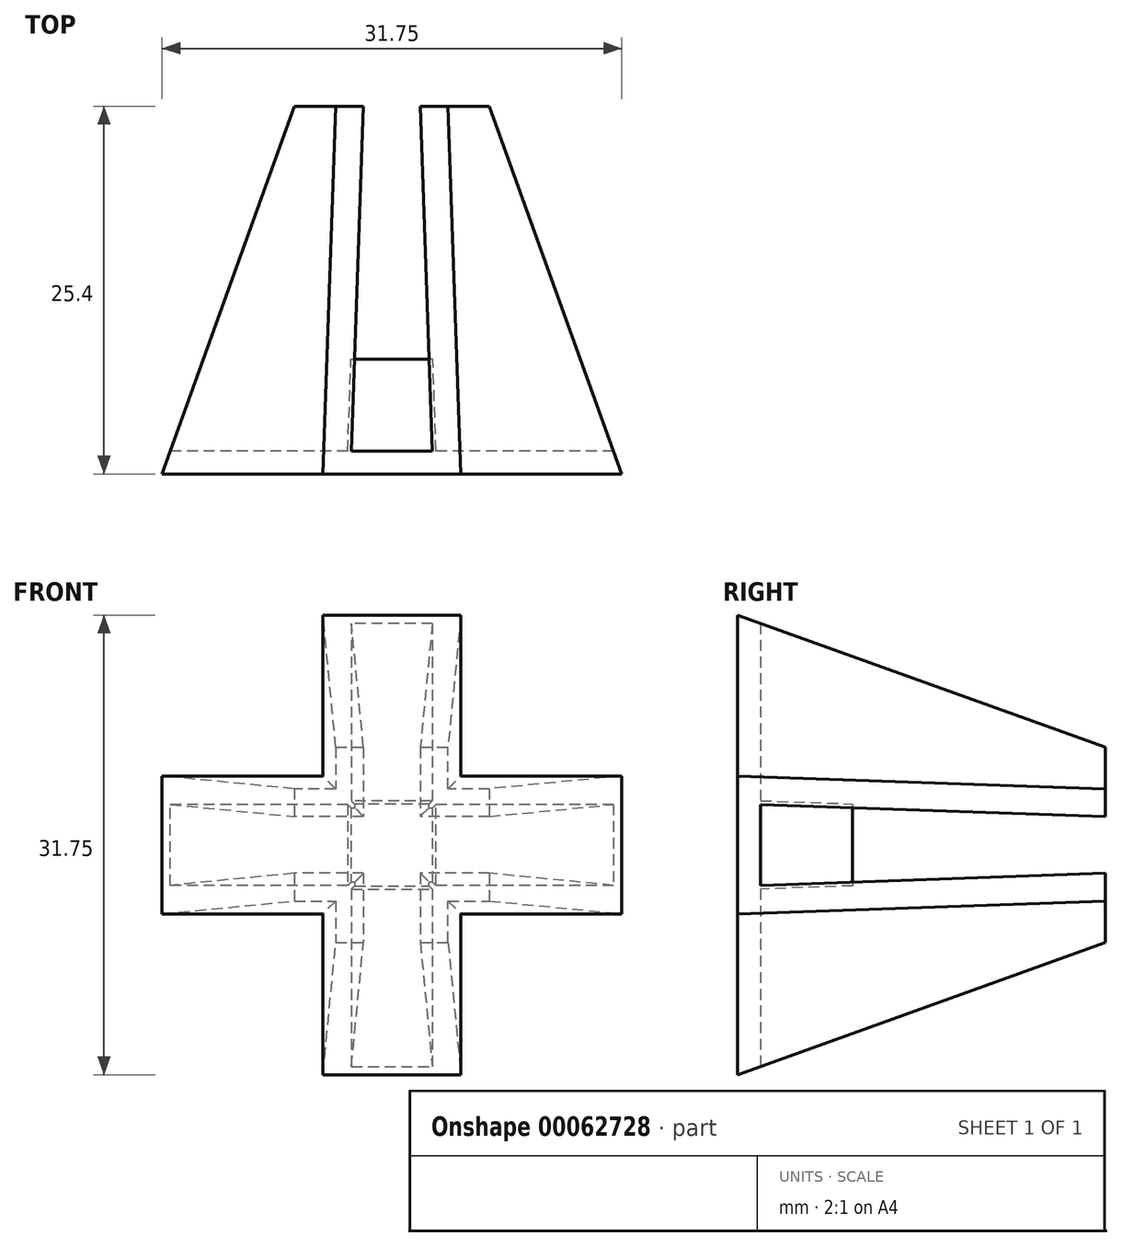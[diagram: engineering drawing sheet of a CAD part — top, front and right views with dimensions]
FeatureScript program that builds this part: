
annotation { "Feature Type Name" : "Feature", "Feature Type Description" : "" }
export const myFeature = defineFeature(function(context is Context, id is Id, definition is map)
    precondition{}
    {
        {
            var Q0;
            Q0=qCreatedBy(makeId("Front.planeOp"),FACE);
            var sketch = newSketch(context, id + "F0", { "sketchPlane" : qUnion([Q0])});
            skLineSegment(sketch, "E0", {"start": v(0, 31.75) * mm, "end": v(9.53, 31.75) * mm});
            skLineSegment(sketch, "E1", {"start": v(9.53, 31.75) * mm, "end": v(9.52, 20.64) * mm});
            skLineSegment(sketch, "E2", {"start": v(9.52, 20.64) * mm, "end": v(20.64, 20.64) * mm});
            skLineSegment(sketch, "E3", {"start": v(20.64, 20.64) * mm, "end": v(20.64, 11.11) * mm});
            skLineSegment(sketch, "E4", {"start": v(20.64, 11.11) * mm, "end": v(9.52, 11.11) * mm});
            skLineSegment(sketch, "E5", {"start": v(9.52, 11.11) * mm, "end": v(9.52, 0) * mm});
            skLineSegment(sketch, "E6", {"start": v(9.52, 0) * mm, "end": v(0, 0) * mm});
            skLineSegment(sketch, "E7", {"start": v(0, 0) * mm, "end": v(0, 11.11) * mm});
            skLineSegment(sketch, "E8", {"start": v(0, 11.11) * mm, "end": v(-11.11, 11.11) * mm});
            skLineSegment(sketch, "E9", {"start": v(-11.11, 11.11) * mm, "end": v(-11.11, 20.64) * mm});
            skLineSegment(sketch, "E10", {"start": v(-11.11, 20.64) * mm, "end": v(0, 20.64) * mm});
            skLineSegment(sketch, "E11", {"start": v(0, 20.64) * mm, "end": v(0, 31.75) * mm});
            skSolve(sketch);
        }
        {
            var Q0;
            Q0=makeQuery(id+"F0.imprint","IMPRINT",FACE,{"disambiguationData":[TD([[makeQuery(id+"F0.imprint","IMPRINT",EDGE,{"derivedFrom":sQuery(id+"F0.wireOp",EDGE,"E0")}),-1.0]])]});
            extrude(context, id + "F1", {"entities" : qUnion([Q0]), "oppositeDirection" : true, "depth" : 25.4 * mm, "hasDraft" : true, "draftAngle" : 2 * degree, "draftPullDirection" : true});
        }
        {
            var Q0;
            Q0=qCreatedBy(makeId("Top.planeOp"),FACE);
            var sketch = newSketch(context, id + "F2", { "sketchPlane" : qUnion([Q0])});
            skLineSegment(sketch, "E12", {"start": v(1.97, 1.59) * mm, "end": v(7.56, 1.59) * mm});
            skLineSegment(sketch, "E13", {"start": v(4.76, 1.59) * mm, "end": v(4.76, 0) * mm, "construction": true});
            skLineSegment(sketch, "E14", {"start": v(1.97, 1.59) * mm, "end": v(2.8, 25.4) * mm});
            skLineSegment(sketch, "E15", {"start": v(2.8, 25.4) * mm, "end": v(6.72, 25.4) * mm});
            skLineSegment(sketch, "E16", {"start": v(6.72, 25.4) * mm, "end": v(7.56, 1.59) * mm});
            skSolve(sketch);
        }
        {
            var Q0;
            Q0=makeQuery(id+"F2.imprint","IMPRINT",FACE,{"disambiguationData":[TD([[makeQuery(id+"F2.imprint","IMPRINT",EDGE,{"derivedFrom":sQuery(id+"F2.wireOp",EDGE,"E12")}),1.0]])]});
            extrude(context, id + "F3", {"entities" : qUnion([Q0]), "operationType" : NewBodyOperationType.REMOVE, "endBound" : BoundingType.THROUGH_ALL, "depth" : 25.4 * mm});
        }
        {
            var Q0;
            Q0=qCreatedBy(makeId("Right.planeOp"),FACE);
            var sketch = newSketch(context, id + "F4", { "sketchPlane" : qUnion([Q0])});
            skLineSegment(sketch, "E17", {"start": v(1.59, 18.67) * mm, "end": v(1.59, 13.08) * mm});
            skLineSegment(sketch, "E18", {"start": v(1.59, 13.08) * mm, "end": v(25.4, 13.91) * mm});
            skLineSegment(sketch, "E19", {"start": v(25.4, 13.91) * mm, "end": v(25.4, 17.84) * mm});
            skLineSegment(sketch, "E20", {"start": v(25.4, 17.84) * mm, "end": v(1.59, 18.67) * mm});
            skLineSegment(sketch, "E21", {"start": v(1.59, 18.67) * mm, "end": v(0, 20.64) * mm, "construction": true});
            skLineSegment(sketch, "E22", {"start": v(1.59, 13.08) * mm, "end": v(0, 11.11) * mm, "construction": true});
            skSolve(sketch);
        }
        {
            var Q0;
            Q0 = qSketchRegion(id + "F4", true);
            extrude(context, id + "F5", {"entities" : qUnion([Q0]), "operationType" : NewBodyOperationType.REMOVE, "endBound" : BoundingType.THROUGH_ALL, "depth" : 25.4 * mm, "hasSecondDirection" : true, "secondDirectionBound" : SecondDirectionBoundingType.THROUGH_ALL, "secondDirectionOppositeDirection" : true, "secondDirectionDepth" : 25.4 * mm});
        }
        {
            var Q0;
            Q0=makeQuery(id+"F5.boolean.opBoolean","MERGE",FACE,{"derivedFrom":[makeQuery(id+"F3.boolean.opBoolean","COPY",FACE,{"derivedFrom":makeQuery(id+"F3.opExtrude","SWEPT_FACE",FACE,{"disambiguationData":[OSD([sQuery(id+"F2.wireOp",EDGE,"E12")])]})}),makeQuery(id+"F5.opExtrude","SWEPT_FACE",FACE,{"disambiguationData":[OSD([sQuery(id+"F4.wireOp",EDGE,"E17")])]})]});
            var sketch = newSketch(context, id + "F6", { "sketchPlane" : qUnion([Q0])});
            skLineSegment(sketch, "E23", {"start": v(-2.8, 17.84) * mm, "end": v(-6.72, 13.91) * mm, "construction": true});
            skLineSegment(sketch, "E24.rect.bottom", {"start": v(-1.71, 12.83) * mm, "end": v(-7.81, 12.83) * mm});
            skLineSegment(sketch, "E24.rect.top", {"start": v(-1.71, 18.92) * mm, "end": v(-7.81, 18.92) * mm});
            skLineSegment(sketch, "E24.rect.left", {"start": v(-1.71, 12.83) * mm, "end": v(-1.71, 18.92) * mm});
            skLineSegment(sketch, "E24.rect.right", {"start": v(-7.81, 12.83) * mm, "end": v(-7.81, 18.92) * mm});
            skPoint(sketch, "E24.rect.middle", {"position": v(-4.76, 15.88) * mm});
            skSolve(sketch);
        }
        {
            var Q0;
            Q0 = qSketchRegion(id + "F6", true);
            extrude(context, id + "F7", {"entities" : qUnion([Q0]), "operationType" : NewBodyOperationType.ADD, "depth" : 6.35 * mm, "hasDraft" : true, "draftAngle" : 2 * degree, "draftPullDirection" : true});
        }
        {
            var Q0;
            Q0=qCreatedBy(makeId("Top.planeOp"),FACE);
            var sketch = newSketch(context, id + "F8", { "sketchPlane" : qUnion([Q0])});
            skLineSegment(sketch, "E25", {"start": v(-11.11, 0) * mm, "end": v(-1.98, 25.4) * mm});
            skLineSegment(sketch, "E26", {"start": v(-1.98, 25.4) * mm, "end": v(11.5, 25.4) * mm});
            skLineSegment(sketch, "E27", {"start": v(11.5, 25.4) * mm, "end": v(20.64, 0) * mm});
            skLineSegment(sketch, "E28", {"start": v(20.64, 0) * mm, "end": v(-11.11, 0) * mm});
            skLineSegment(sketch, "E29.rect.bottom", {"start": v(34.87, 38.37) * mm, "end": v(-25.8, 38.37) * mm});
            skLineSegment(sketch, "E29.rect.top", {"start": v(34.87, -11.76) * mm, "end": v(-25.8, -11.76) * mm});
            skLineSegment(sketch, "E29.rect.left", {"start": v(34.87, 38.37) * mm, "end": v(34.87, -11.76) * mm});
            skLineSegment(sketch, "E29.rect.right", {"start": v(-25.8, 38.37) * mm, "end": v(-25.8, -11.76) * mm});
            skPoint(sketch, "E29.rect.middle", {"position": v(4.53, 13.3) * mm});
            skSolve(sketch);
        }
        {
            var Q0;
            Q0=makeQuery(id+"F8.imprint","IMPRINT",FACE,{"disambiguationData":[TD([[makeQuery(id+"F8.imprint","IMPRINT",EDGE,{"derivedFrom":sQuery(id+"F8.wireOp",EDGE,"E25")}),1.0]])]});
            extrude(context, id + "F9", {"entities" : qUnion([Q0]), "operationType" : NewBodyOperationType.REMOVE, "endBound" : BoundingType.THROUGH_ALL, "depth" : 25.4 * mm});
        }
        {
            var Q0;
            Q0=qCreatedBy(makeId("Right.planeOp"),FACE);
            var sketch = newSketch(context, id + "F10", { "sketchPlane" : qUnion([Q0])});
            skLineSegment(sketch, "E30", {"start": v(0, 31.75) * mm, "end": v(25.4, 22.61) * mm});
            skLineSegment(sketch, "E31", {"start": v(25.4, 22.61) * mm, "end": v(25.4, 9.14) * mm});
            skLineSegment(sketch, "E32", {"start": v(25.4, 9.14) * mm, "end": v(0, 0) * mm});
            skLineSegment(sketch, "E33", {"start": v(0, 0) * mm, "end": v(0, 31.75) * mm});
            skLineSegment(sketch, "E34.rect.bottom", {"start": v(-6.67, -4.93) * mm, "end": v(30.37, -4.93) * mm});
            skLineSegment(sketch, "E34.rect.top", {"start": v(-6.67, 36.51) * mm, "end": v(30.37, 36.51) * mm});
            skLineSegment(sketch, "E34.rect.left", {"start": v(-6.67, -4.93) * mm, "end": v(-6.67, 36.51) * mm});
            skLineSegment(sketch, "E34.rect.right", {"start": v(30.37, -4.93) * mm, "end": v(30.37, 36.51) * mm});
            skPoint(sketch, "E34.rect.middle", {"position": v(11.85, 15.8) * mm});
            skSolve(sketch);
        }
        {
            var Q0;
            Q0=makeQuery(id+"F10.imprint","IMPRINT",FACE,{"disambiguationData":[TD([[makeQuery(id+"F10.imprint","IMPRINT",EDGE,{"derivedFrom":sQuery(id+"F10.wireOp",EDGE,"E30")}),1.0]])]});
            extrude(context, id + "F11", {"entities" : qUnion([Q0]), "operationType" : NewBodyOperationType.REMOVE, "endBound" : BoundingType.THROUGH_ALL, "oppositeDirection" : true, "depth" : 25.4 * mm, "hasSecondDirection" : true, "secondDirectionBound" : SecondDirectionBoundingType.THROUGH_ALL, "secondDirectionOppositeDirection" : false, "secondDirectionDepth" : 25.4 * mm});
        }
    });
